# Revit family: xSpout-American_Standard-Studio_S-8888_Series
name_source: partatom
category: Plumbing Fixtures
revit_build: Autodesk Revit 2014 (Build: 20130308_1515(x64)
units: mm (PartAtom-declared; Revit-internal decimal feet)

## types (4) — shared parameters
Assembly Code = D2020300
CW Connection = Yes
CWFU = 3
Default Elevation = 21"
Finish = Metal-American Standard-002-Polished Chrome
HW Connection = Yes
HWFU = 3
Installation Type = Wall Mounted
Length = 6 1/8"
Manufacturer = American Standard
Material = Metal-American Standard-002-Polished Chrome
Price = Prices may vary. Please consult Manufacturer Representative for most up-to-date price list.
Product Page URL = https://www.americanstandard-us.com
URL = https://www.americanstandard-us.com
Vent Connection = No
WFU = 4
Warranty Information = Limited Lifetime Function and Finish Warranty
Waste Connection = Yes
Water Connection Diameter = 1/2"
Water Connection Radius = 1/4"
Width = 2 3/4"

## per-type parameters (varying)
| type | Description | Pop-up handle |
| 8888.316 | Studio S Slip-On Non-Diverter Tub Spout | No |
| 8888.317 | Studio S Non-Diverter 1/2 IPS Tub Spout | No |
| 8888.318 | Studio S Slip-On-Diverter Tub Spout | Yes |
| 8888.319 | Studio S Diverter 1/2 IPS Tub Spout | Yes |

note: column(s) folded — value = type name in every type: Model

## geometry (parser evidence)
native form markers: Sweep x3
no freeform markers — native parametric forms only
